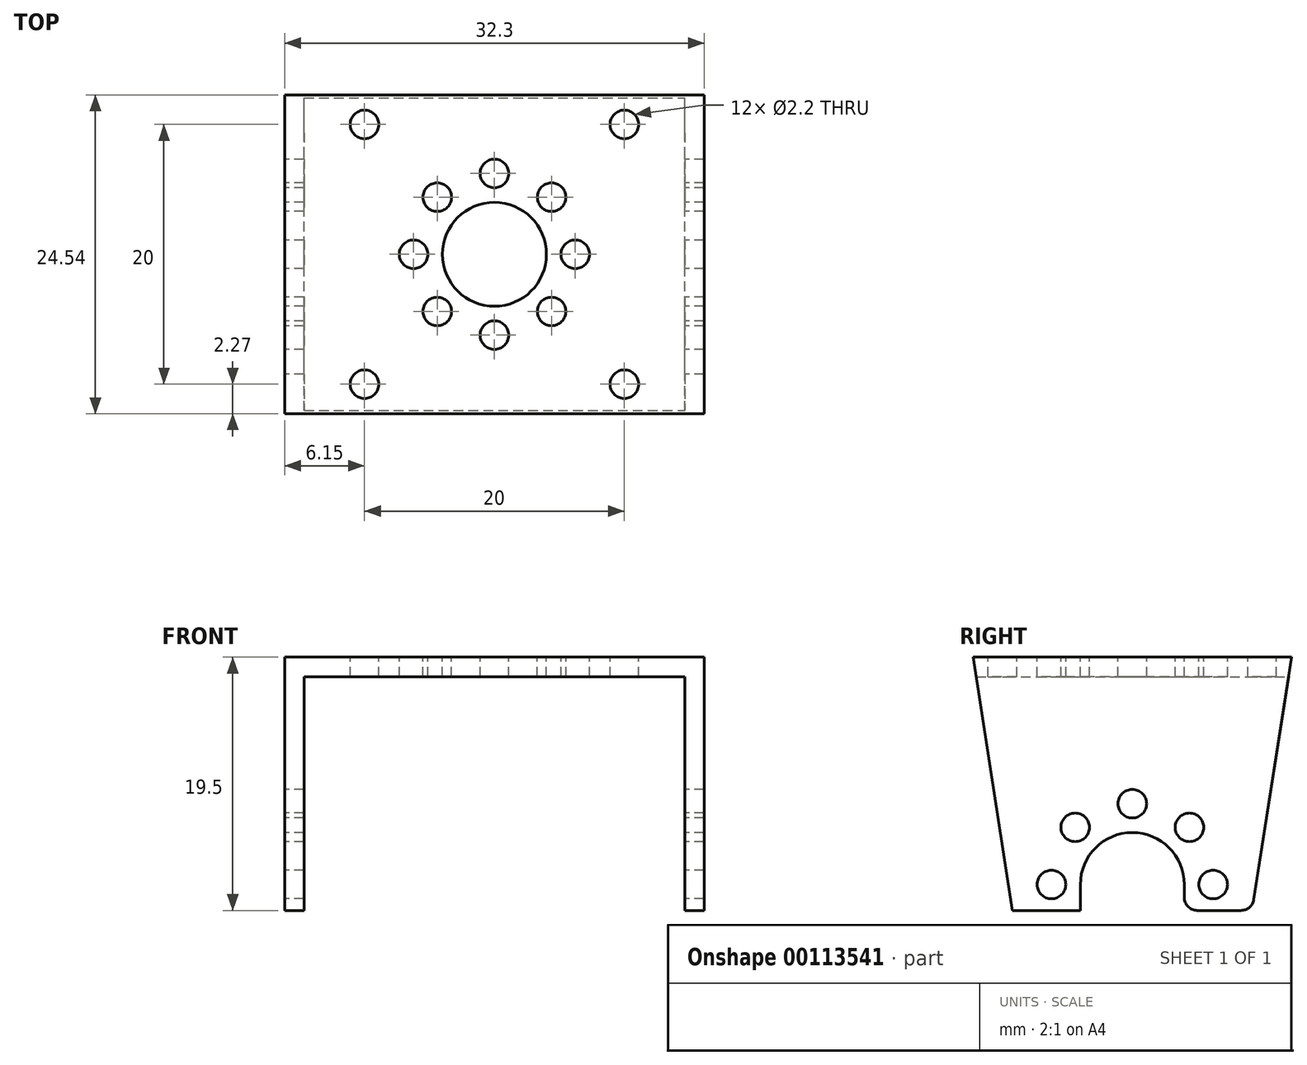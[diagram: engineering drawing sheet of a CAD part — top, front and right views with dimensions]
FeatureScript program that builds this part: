
annotation { "Feature Type Name" : "Feature", "Feature Type Description" : "" }
export const myFeature = defineFeature(function(context is Context, id is Id, definition is map)
    precondition{}
    {
        {
            var Q0;
            Q0=qCreatedBy(makeId("Front.planeOp"),FACE);
            var sketch = newSketch(context, id + "F0", { "sketchPlane" : qUnion([Q0])});
            skLineSegment(sketch, "E0.bottom", {"start": v(0, 0) * mm, "end": v(1.5, 0) * mm});
            skLineSegment(sketch, "E0.top", {"start": v(0, 19.5) * mm, "end": v(32.3, 19.5) * mm});
            skLineSegment(sketch, "E0.left", {"start": v(0, 0) * mm, "end": v(0, 19.5) * mm});
            skLineSegment(sketch, "E0.right", {"start": v(32.3, 0) * mm, "end": v(32.3, 19.5) * mm});
            skLineSegment(sketch, "E1.top", {"start": v(1.5, 18) * mm, "end": v(30.8, 18) * mm});
            skLineSegment(sketch, "E1.left", {"start": v(1.5, 0) * mm, "end": v(1.5, 18) * mm});
            skLineSegment(sketch, "E1.right", {"start": v(30.8, 0) * mm, "end": v(30.8, 18) * mm});
            skLineSegment(sketch, "E2.trimOffspring", {"start": v(30.8, 0) * mm, "end": v(32.3, 0) * mm});
            skSolve(sketch);
        }
        {
            var Q0;
            Q0=qSketchRegion(id+"F0",true);
            extrude(context, id + "F1", {"entities" : qUnion([Q0]), "depth" : 25 * mm});
        }
        {
            var Q0;
            Q0=makeQuery(id+"F1.opExtrude","SWEPT_FACE",FACE,{"disambiguationData":[OSD([sQuery(id+"F0.wireOp",EDGE,"E0.left")])]});
            var sketch = newSketch(context, id + "F2", { "sketchPlane" : qUnion([Q0])});
            skArc(sketch, "E3", {"start": v(16.5, 2) * mm, "mid": v(12.5, 6) * mm, "end": v(8.5, 2) * mm});
            skCircle(sketch, "E4", {"center": v(18.72, 2) * mm, "radius": 1.1 * mm});
            skCircle(sketch, "E5.1.0", {"center": v(16.9, 6.4) * mm, "radius": 1.1 * mm});
            skCircle(sketch, "E5.2.0", {"center": v(12.5, 8.22) * mm, "radius": 1.1 * mm});
            skCircle(sketch, "E5.3.0", {"center": v(8.1, 6.4) * mm, "radius": 1.1 * mm});
            skCircle(sketch, "E5.4.0", {"center": v(6.28, 2) * mm, "radius": 1.1 * mm});
            skLineSegment(sketch, "E6", {"start": v(8.5, 2) * mm, "end": v(8.5, 0) * mm});
            skLineSegment(sketch, "E7", {"start": v(16.5, 2) * mm, "end": v(16.5, 0) * mm});
            skLineSegment(sketch, "E8", {"start": v(8.5, 0) * mm, "end": v(16.5, 0) * mm});
            skLineSegment(sketch, "E9", {"start": v(12.5, 19.5) * mm, "end": v(12.5, 0) * mm, "construction": true});
            skPoint(sketch, "E10", {"position": v(12.5, 0) * mm});
            skLineSegment(sketch, "E11", {"start": v(3.28, 0) * mm, "end": v(0, 21) * mm});
            skLineSegment(sketch, "E12", {"start": v(3.28, 0) * mm, "end": v(0, 0) * mm});
            skLineSegment(sketch, "E13", {"start": v(0, 0) * mm, "end": v(0, 21) * mm});
            skLineSegment(sketch, "E14.MirrorCS", {"start": v(25, 0) * mm, "end": v(25, 21) * mm});
            skLineSegment(sketch, "E15.MirrorCS", {"start": v(21.72, 0) * mm, "end": v(25, 21) * mm});
            skLineSegment(sketch, "E16.MirrorCS", {"start": v(21.72, 0) * mm, "end": v(25, 0) * mm});
            skSolve(sketch);
        }
        {
            var Q0;
            Q0=qSketchRegion(id+"F2",true);
            extrude(context, id + "F3", {"entities" : qUnion([Q0]), "operationType" : NewBodyOperationType.REMOVE, "endBound" : BoundingType.THROUGH_ALL, "oppositeDirection" : true, "depth" : 25 * mm});
        }
        {
            var Q0;
            Q0=makeQuery(id+"F1.opExtrude","SWEPT_FACE",FACE,{"disambiguationData":[OSD([sQuery(id+"F0.wireOp",EDGE,"E0.top")])]});
            var sketch = newSketch(context, id + "F4", { "sketchPlane" : qUnion([Q0])});
            skLineSegment(sketch, "E17", {"start": v(16.15, -0.23) * mm, "end": v(16.15, -24.77) * mm, "construction": true});
            skLineSegment(sketch, "E18", {"start": v(0, -12.5) * mm, "end": v(32.3, -12.5) * mm, "construction": true});
            skCircle(sketch, "E19", {"center": v(6.15, -2.5) * mm, "radius": 1.1 * mm});
            skCircle(sketch, "E20.MirrorC", {"center": v(26.15, -2.5) * mm, "radius": 1.1 * mm});
            skCircle(sketch, "E21.MirrorC", {"center": v(6.15, -22.5) * mm, "radius": 1.1 * mm});
            skCircle(sketch, "E22.MirrorC", {"center": v(26.15, -22.5) * mm, "radius": 1.1 * mm});
            skCircle(sketch, "E23", {"center": v(16.15, -12.5) * mm, "radius": 4 * mm});
            skLineSegment(sketch, "E24.bottom", {"start": v(20.55, -16.9) * mm, "end": v(11.75, -16.9) * mm, "construction": true});
            skLineSegment(sketch, "E24.top", {"start": v(20.55, -8.1) * mm, "end": v(11.75, -8.1) * mm, "construction": true});
            skLineSegment(sketch, "E24.left", {"start": v(20.55, -16.9) * mm, "end": v(20.55, -8.1) * mm, "construction": true});
            skLineSegment(sketch, "E24.right", {"start": v(11.75, -16.9) * mm, "end": v(11.75, -8.1) * mm, "construction": true});
            skCircle(sketch, "E25", {"center": v(11.75, -8.1) * mm, "radius": 1.1 * mm});
            skCircle(sketch, "E26.1.0", {"center": v(9.93, -12.5) * mm, "radius": 1.1 * mm});
            skCircle(sketch, "E26.2.0", {"center": v(11.75, -16.9) * mm, "radius": 1.1 * mm});
            skCircle(sketch, "E26.3.0", {"center": v(16.15, -18.72) * mm, "radius": 1.1 * mm});
            skCircle(sketch, "E27.1.4.0", {"center": v(20.55, -16.9) * mm, "radius": 1.1 * mm});
            skCircle(sketch, "E27.1.5.0", {"center": v(22.37, -12.5) * mm, "radius": 1.1 * mm});
            skCircle(sketch, "E27.1.6.0", {"center": v(20.55, -8.1) * mm, "radius": 1.1 * mm});
            skCircle(sketch, "E27.1.7.0", {"center": v(16.15, -6.28) * mm, "radius": 1.1 * mm});
            skLineSegment(sketch, "E28.0", {"start": v(0, -24.77) * mm, "end": v(0, -0.23) * mm, "construction": true});
            skLineSegment(sketch, "E29.0", {"start": v(0, -0.23) * mm, "end": v(32.3, -0.23) * mm, "construction": true});
            skLineSegment(sketch, "E30.0", {"start": v(32.3, -24.77) * mm, "end": v(32.3, -0.23) * mm, "construction": true});
            skLineSegment(sketch, "E31.0", {"start": v(0, -24.77) * mm, "end": v(32.3, -24.77) * mm, "construction": true});
            skPoint(sketch, "E32", {"position": v(16.15, -24.77) * mm});
            skPoint(sketch, "E33", {"position": v(16.15, -0.23) * mm});
            skSolve(sketch);
        }
        {
            var Q0;
            Q0=qSketchRegion(id+"F4",true);
            extrude(context, id + "F5", {"entities" : qUnion([Q0]), "operationType" : NewBodyOperationType.REMOVE, "endBound" : BoundingType.UP_TO_NEXT, "oppositeDirection" : true, "depth" : 25 * mm});
        }
        {
            var Q0;
            Q0=makeQuery(id+"F3.boolean.opBoolean","COPY",EDGE,{"disambiguationData":[OD(0.0)],"derivedFrom":makeQuery(id+"F3.opExtrude","SWEPT_EDGE",EDGE,{"disambiguationData":[OSD([sQuery(id+"F0.wireOp",EDGE,"E0.bottom"),sQuery(id+"F0.wireOp",EDGE,"E0.left"),sQuery(id+"F2.wireOp",EDGE,"E11"),sQuery(id+"F2.wireOp",EDGE,"E12")])]})});
            var Q1;
            Q1=makeQuery(id+"F3.boolean.opBoolean","COPY",EDGE,{"disambiguationData":[OD(0.0)],"derivedFrom":makeQuery(id+"F3.opExtrude","SWEPT_EDGE",EDGE,{"disambiguationData":[OSD([sQuery(id+"F0.wireOp",EDGE,"E0.bottom"),sQuery(id+"F0.wireOp",EDGE,"E0.left"),sQuery(id+"F2.wireOp",EDGE,"E6"),sQuery(id+"F2.wireOp",EDGE,"E8")])]})});
            var Q2;
            Q2=makeQuery(id+"F3.boolean.opBoolean","COPY",EDGE,{"disambiguationData":[OD(0.0)],"derivedFrom":makeQuery(id+"F3.opExtrude","SWEPT_EDGE",EDGE,{"disambiguationData":[OSD([sQuery(id+"F0.wireOp",EDGE,"E0.bottom"),sQuery(id+"F0.wireOp",EDGE,"E0.left"),sQuery(id+"F2.wireOp",EDGE,"E7"),sQuery(id+"F2.wireOp",EDGE,"E8")])]})});
            var Q3;
            Q3=makeQuery(id+"F3.boolean.opBoolean","COPY",EDGE,{"disambiguationData":[OD(0.0)],"derivedFrom":makeQuery(id+"F3.opExtrude","SWEPT_EDGE",EDGE,{"disambiguationData":[OSD([sQuery(id+"F0.wireOp",EDGE,"E0.bottom"),sQuery(id+"F0.wireOp",EDGE,"E0.left"),sQuery(id+"F2.wireOp",EDGE,"E15.MirrorCS"),sQuery(id+"F2.wireOp",EDGE,"E16.MirrorCS")])]})});
            var Q4;
            Q4=makeQuery(id+"F3.boolean.opBoolean","COPY",EDGE,{"disambiguationData":[OD(1.0)],"derivedFrom":makeQuery(id+"F3.opExtrude","SWEPT_EDGE",EDGE,{"disambiguationData":[OSD([sQuery(id+"F0.wireOp",EDGE,"E0.bottom"),sQuery(id+"F0.wireOp",EDGE,"E0.left"),sQuery(id+"F2.wireOp",EDGE,"E11"),sQuery(id+"F2.wireOp",EDGE,"E12")])]})});
            var Q5;
            Q5=makeQuery(id+"F3.boolean.opBoolean","COPY",EDGE,{"disambiguationData":[OD(1.0)],"derivedFrom":makeQuery(id+"F3.opExtrude","SWEPT_EDGE",EDGE,{"disambiguationData":[OSD([sQuery(id+"F0.wireOp",EDGE,"E0.bottom"),sQuery(id+"F0.wireOp",EDGE,"E0.left"),sQuery(id+"F2.wireOp",EDGE,"E6"),sQuery(id+"F2.wireOp",EDGE,"E8")])]})});
            var Q6;
            Q6=makeQuery(id+"F3.boolean.opBoolean","COPY",EDGE,{"disambiguationData":[OD(1.0)],"derivedFrom":makeQuery(id+"F3.opExtrude","SWEPT_EDGE",EDGE,{"disambiguationData":[OSD([sQuery(id+"F0.wireOp",EDGE,"E0.bottom"),sQuery(id+"F0.wireOp",EDGE,"E0.left"),sQuery(id+"F2.wireOp",EDGE,"E7"),sQuery(id+"F2.wireOp",EDGE,"E8")])]})});
            var Q7;
            Q7=makeQuery(id+"F3.boolean.opBoolean","COPY",EDGE,{"disambiguationData":[OD(1.0)],"derivedFrom":makeQuery(id+"F3.opExtrude","SWEPT_EDGE",EDGE,{"disambiguationData":[OSD([sQuery(id+"F0.wireOp",EDGE,"E0.bottom"),sQuery(id+"F0.wireOp",EDGE,"E0.left"),sQuery(id+"F2.wireOp",EDGE,"E15.MirrorCS"),sQuery(id+"F2.wireOp",EDGE,"E16.MirrorCS")])]})});
            fillet(context, id + "F6", {"entities" : qUnion([Q0, Q1, Q2, Q3, Q4, Q5, Q6, Q7]), "radius" : 1 * mm, "tangentPropagation" : true, "allowEdgeOverflow" : false});
        }
    });
